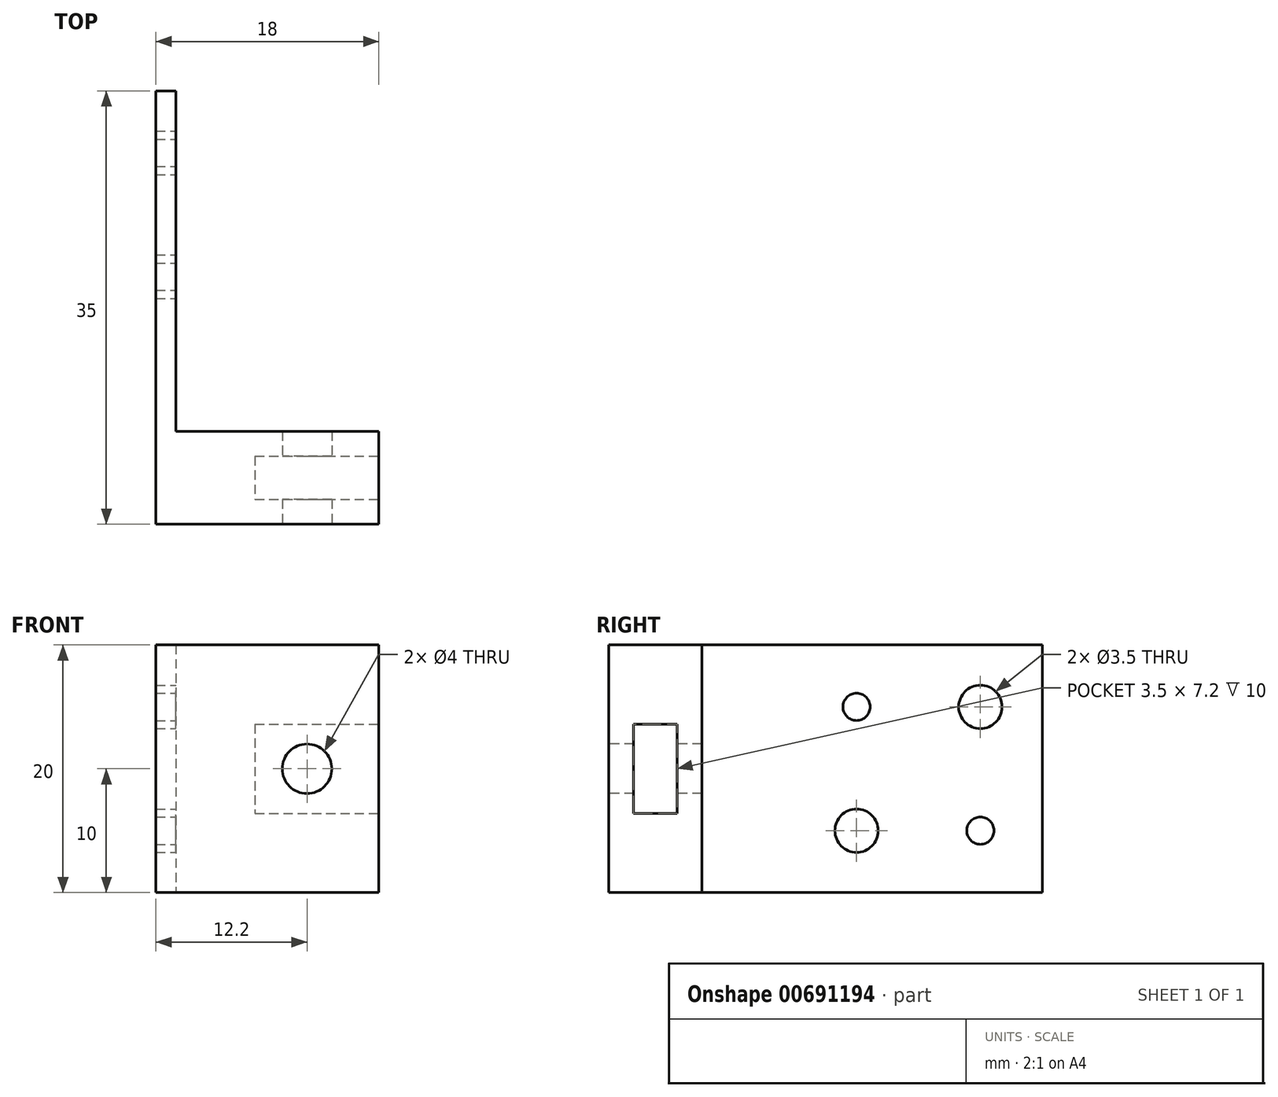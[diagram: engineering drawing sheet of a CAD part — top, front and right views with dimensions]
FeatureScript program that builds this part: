
annotation { "Feature Type Name" : "Feature", "Feature Type Description" : "" }
export const myFeature = defineFeature(function(context is Context, id is Id, definition is map)
    precondition{}
    {
        {
            var Q0;
            Q0=qCreatedBy(makeId("Right.planeOp"),FACE);
            var sketch = newSketch(context, id + "F0", { "sketchPlane" : qUnion([Q0])});
            skLineSegment(sketch, "E0.bottom", {"start": v(10, 10) * mm, "end": v(-10, 10) * mm});
            skLineSegment(sketch, "E0.top", {"start": v(10, -10) * mm, "end": v(-10, -10) * mm});
            skLineSegment(sketch, "E0.left", {"start": v(10, 10) * mm, "end": v(10, -10) * mm});
            skLineSegment(sketch, "E0.right", {"start": v(-10, 10) * mm, "end": v(-10, -10) * mm});
            skPoint(sketch, "E0.middle", {"position": v(0, 0) * mm});
            skLineSegment(sketch, "E1", {"start": v(-10, 10) * mm, "end": v(0, 0) * mm, "construction": true});
            skCircle(sketch, "E2", {"center": v(-5, 5) * mm, "radius": 1.1 * mm});
            skCircle(sketch, "E3", {"center": v(-5, 5) * mm, "radius": 1.75 * mm});
            skCircle(sketch, "E4.MirrorC", {"center": v(5, 5) * mm, "radius": 1.75 * mm});
            skCircle(sketch, "E5.MirrorC", {"center": v(5, 5) * mm, "radius": 1.1 * mm});
            skCircle(sketch, "E6.MirrorC", {"center": v(-5, -5) * mm, "radius": 1.75 * mm});
            skCircle(sketch, "E7.MirrorC", {"center": v(-5, -5) * mm, "radius": 1.1 * mm});
            skCircle(sketch, "E8.MirrorC", {"center": v(5, -5) * mm, "radius": 1.1 * mm});
            skCircle(sketch, "E9.MirrorC", {"center": v(5, -5) * mm, "radius": 1.75 * mm});
            skLineSegment(sketch, "E10.bottom", {"start": v(-10, 10) * mm, "end": v(-25, 10) * mm});
            skLineSegment(sketch, "E10.top", {"start": v(-10, -10) * mm, "end": v(-25, -10) * mm});
            skLineSegment(sketch, "E10.right", {"start": v(-25, 10) * mm, "end": v(-25, -10) * mm});
            skLineSegment(sketch, "E11", {"start": v(-25, 10) * mm, "end": v(-17.5, 10) * mm, "construction": true});
            skLineSegment(sketch, "E12", {"start": v(-17.5, 10) * mm, "end": v(-17.5, -10) * mm});
            skSolve(sketch);
        }
        {
            var Q0;
            Q0=makeQuery(id+"F0.imprint","IMPRINT",FACE,{"disambiguationData":[TD([[makeQuery(id+"F0.imprint","IMPRINT",EDGE,{"derivedFrom":sQuery(id+"F0.wireOp",EDGE,"E0.bottom")}),1.0]])]});
            var Q1;
            Q1=makeQuery(id+"F0.imprint","IMPRINT",FACE,{"disambiguationData":[TD([[makeQuery(id+"F0.imprint","IMPRINT",EDGE,{"derivedFrom":sQuery(id+"F0.wireOp",EDGE,"E2")}),-1.0]])]});
            var Q2;
            Q2=makeQuery(id+"F0.imprint","IMPRINT",FACE,{"disambiguationData":[TD([[makeQuery(id+"F0.imprint","IMPRINT",EDGE,{"derivedFrom":sQuery(id+"F0.wireOp",EDGE,"E4.MirrorC")}),-1.0]])]});
            var Q3;
            Q3=makeQuery(id+"F0.imprint","IMPRINT",FACE,{"disambiguationData":[TD([[makeQuery(id+"F0.imprint","IMPRINT",EDGE,{"derivedFrom":sQuery(id+"F0.wireOp",EDGE,"E8.MirrorC")}),-1.0]])]});
            var Q4;
            Q4=makeQuery(id+"F0.imprint","IMPRINT",FACE,{"disambiguationData":[TD([[makeQuery(id+"F0.imprint","IMPRINT",EDGE,{"derivedFrom":sQuery(id+"F0.wireOp",EDGE,"E6.MirrorC")}),-1.0]])]});
            extrude(context, id + "F1", {"entities" : qUnion([Q0, Q1, Q2, Q3, Q4]), "oppositeDirection" : true, "depth" : 3 * mm, "offsetDistance" : 25 * mm});
        }
        {
            var Q0;
            Q0=makeQuery(id+"F0.imprint","IMPRINT",FACE,{"disambiguationData":[TD([[makeQuery(id+"F0.imprint","IMPRINT",EDGE,{"derivedFrom":sQuery(id+"F0.wireOp",EDGE,"E2")}),-1.0]])]});
            var Q1;
            Q1=makeQuery(id+"F0.imprint","IMPRINT",FACE,{"disambiguationData":[TD([[makeQuery(id+"F0.imprint","IMPRINT",EDGE,{"derivedFrom":sQuery(id+"F0.wireOp",EDGE,"E4.MirrorC")}),-1.0]])]});
            var Q2;
            Q2=makeQuery(id+"F0.imprint","IMPRINT",FACE,{"disambiguationData":[TD([[makeQuery(id+"F0.imprint","IMPRINT",EDGE,{"derivedFrom":sQuery(id+"F0.wireOp",EDGE,"E8.MirrorC")}),-1.0]])]});
            var Q3;
            Q3=makeQuery(id+"F0.imprint","IMPRINT",FACE,{"disambiguationData":[TD([[makeQuery(id+"F0.imprint","IMPRINT",EDGE,{"derivedFrom":sQuery(id+"F0.wireOp",EDGE,"E6.MirrorC")}),-1.0]])]});
            extrude(context, id + "F2", {"entities" : qUnion([Q0, Q1, Q2, Q3]), "operationType" : NewBodyOperationType.REMOVE, "oppositeDirection" : true, "depth" : 1.4 * mm, "offsetDistance" : 25 * mm});
        }
        {
            var Q0;
            {var subQ0=sQuery(id+"F0.wireOp",EDGE,"E10.right");Q0=makeQuery(id+"F0.imprint","IMPRINT",FACE,{"disambiguationData":[TD([[makeQuery(id+"F0.imprint","IMPRINT",EDGE,{"derivedFrom":subQ0}),1.0]])]});}
            extrude(context, id + "F3", {"entities" : qUnion([Q0]), "depth" : 15 * mm, "offsetDistance" : 25 * mm});
        }
        {
            var Q0;
            Q0=makeQuery(id+"F3.opExtrude","CAP_FACE",FACE,{"disambiguationData":[OSD([sQuery(id+"F0.wireOp",EDGE,"E10.bottom"),sQuery(id+"F0.wireOp",EDGE,"E10.top"),sQuery(id+"F0.wireOp",EDGE,"E0.right"),sQuery(id+"F0.wireOp",EDGE,"E10.right")])],"isStart":true});
            var Q1;
            Q1=makeQuery(id+"F1.opExtrude","CAP_FACE",FACE,{"disambiguationData":[OSD([sQuery(id+"F0.wireOp",EDGE,"E0.bottom"),sQuery(id+"F0.wireOp",EDGE,"E0.top"),sQuery(id+"F0.wireOp",EDGE,"E0.left"),sQuery(id+"F0.wireOp",EDGE,"E2"),sQuery(id+"F0.wireOp",EDGE,"E5.MirrorC"),sQuery(id+"F0.wireOp",EDGE,"E7.MirrorC"),sQuery(id+"F0.wireOp",EDGE,"E8.MirrorC"),sQuery(id+"F0.wireOp",EDGE,"E0.right")])],"isStart":false});
            extrude(context, id + "F4", {"entities" : qUnion([Q0]), "operationType" : NewBodyOperationType.ADD, "endBound" : BoundingType.UP_TO_SURFACE, "depth" : 25 * mm, "endBoundEntityFace" : qUnion([Q1]), "offsetDistance" : 25 * mm});
        }
        {
            var Q0;
            Q0=makeQuery(id+"F3.opExtrude","CAP_FACE",FACE,{"disambiguationData":[OSD([sQuery(id+"F0.wireOp",EDGE,"E10.bottom"),sQuery(id+"F0.wireOp",EDGE,"E10.top"),sQuery(id+"F0.wireOp",EDGE,"E0.right"),sQuery(id+"F0.wireOp",EDGE,"E10.right")])],"isStart":false});
            var sketch = newSketch(context, id + "F5", { "sketchPlane" : qUnion([Q0])});
            skLineSegment(sketch, "E13.bottom", {"start": v(-19.5, 3.6) * mm, "end": v(-23, 3.6) * mm});
            skLineSegment(sketch, "E13.top", {"start": v(-19.5, -3.6) * mm, "end": v(-23, -3.6) * mm});
            skLineSegment(sketch, "E13.left", {"start": v(-19.5, 3.6) * mm, "end": v(-19.5, -3.6) * mm});
            skLineSegment(sketch, "E13.right", {"start": v(-23, 3.6) * mm, "end": v(-23, -3.6) * mm});
            skPoint(sketch, "E13.middle", {"position": v(-21.25, 0) * mm});
            skLineSegment(sketch, "E14", {"start": v(-25, 0) * mm, "end": v(-17.5, 0) * mm, "construction": true});
            skSolve(sketch);
        }
        {
            var Q0;
            Q0=makeQuery(id+"F5.imprint","IMPRINT",FACE,{"disambiguationData":[TD([[makeQuery(id+"F5.imprint","IMPRINT",EDGE,{"derivedFrom":sQuery(id+"F5.wireOp",EDGE,"E13.bottom")}),1.0]])]});
            extrude(context, id + "F6", {"entities" : qUnion([Q0]), "operationType" : NewBodyOperationType.REMOVE, "oppositeDirection" : true, "depth" : 10 * mm, "offsetDistance" : 25 * mm});
        }
        {
            var Q0;
            {var subQ0=sQuery(id+"F0.wireOp",EDGE,"E10.right");Q0=makeQuery(id+"F4.boolean.opBoolean","MERGE",FACE,{"derivedFrom":[makeQuery(id+"F3.opExtrude","SWEPT_FACE",FACE,{"disambiguationData":[OSD([subQ0])]}),makeQuery(id+"F4.opExtrude","SWEPT_FACE",FACE,{"disambiguationData":[OSD([subQ0])]})]});}
            var sketch = newSketch(context, id + "F7", { "sketchPlane" : qUnion([Q0])});
            skLineSegment(sketch, "E15", {"start": v(15, 0) * mm, "end": v(11.2, 0) * mm, "construction": true});
            skCircle(sketch, "E16", {"center": v(9.2, 0) * mm, "radius": 2 * mm});
            skPoint(sketch, "E17", {"position": v(11.2, 0) * mm});
            skSolve(sketch);
        }
        {
            var Q0;
            Q0 = qSketchRegion(id + "F7", true);
            extrude(context, id + "F8", {"entities" : qUnion([Q0]), "operationType" : NewBodyOperationType.REMOVE, "oppositeDirection" : true, "depth" : 25 * mm, "offsetDistance" : 25 * mm});
        }
        {
            var Q0;
            Q0=makeQuery(id+"F1.opExtrude","SWEPT_FACE",FACE,{"disambiguationData":[OSD([sQuery(id+"F0.wireOp",EDGE,"E0.right")])]});
            extrude(context, id + "F9", {"entities" : qUnion([Q0]), "operationType" : NewBodyOperationType.ADD, "endBound" : BoundingType.UP_TO_NEXT, "depth" : 25 * mm, "offsetDistance" : 25 * mm});
        }
    });
